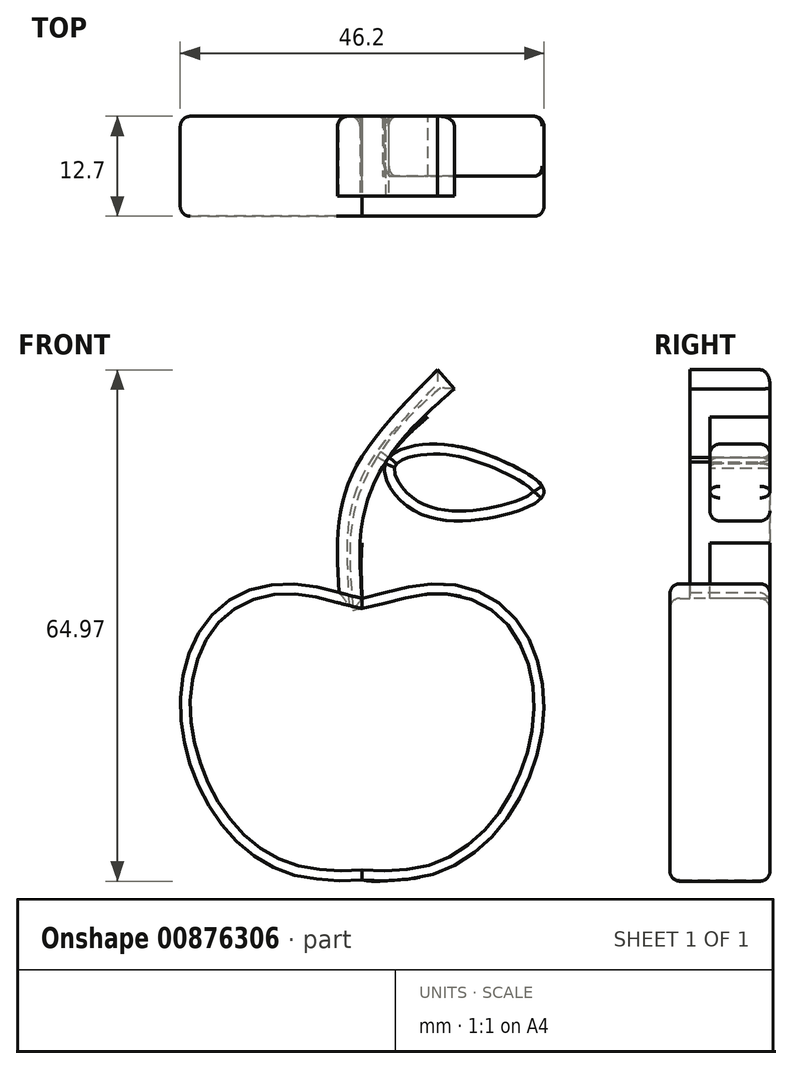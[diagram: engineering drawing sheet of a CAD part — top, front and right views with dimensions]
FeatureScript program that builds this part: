
annotation { "Feature Type Name" : "Feature", "Feature Type Description" : "" }
export const myFeature = defineFeature(function(context is Context, id is Id, definition is map)
    precondition{}
    {
        {
            var Q0;
            Q0=qCreatedBy(makeId("Front.planeOp"),FACE);
            var sketch = newSketch(context, id + "F0", { "sketchPlane" : qUnion([Q0])});
            skFitSpline(sketch, "E0", {"points": [v(0, 29.07) * mm, v(-9.03, 30.9) * mm, v(-18.51, 27.54) * mm, v(-23.1, 15) * mm, v(-17.6, 0) * mm, v(-9.64, -5.81) * mm, v(-4.44, -6.73) * mm, v(0, -6.73) * mm], "startDerivative": vector(-62.06, 12.6) * mm, "endDerivative": vector(36.3, 8.01) * mm});
            skFitSpline(sketch, "E1.MirrorCS", {"points": [v(0, 29.07) * mm, v(9.03, 30.9) * mm, v(18.51, 27.54) * mm, v(23.1, 15) * mm, v(17.6, 0) * mm, v(9.64, -5.81) * mm, v(4.44, -6.73) * mm, v(0, -6.73) * mm], "startDerivative": vector(62.06, 12.6) * mm, "endDerivative": vector(-36.3, 8.01) * mm});
            skFitSpline(sketch, "E2", {"points": [v(0, 29.07) * mm, v(0, 36.1) * mm, v(2.93, 46.2) * mm, v(9.03, 52.63) * mm], "startDerivative": vector(-1.25, 22) * mm, "endDerivative": vector(20.43, 16.63) * mm});
            skFitSpline(sketch, "E3", {"points": [v(2.93, 46.2) * mm, v(9.03, 48.65) * mm, v(18.51, 46.2) * mm, v(23.1, 42.53) * mm, v(17.29, 39.47) * mm, v(6.27, 40.39) * mm, v(2.93, 46.2) * mm]});
            skPoint(sketch, "E4.1.internal.orphan", {"position": v(-2.93, 36.1) * mm});
            skPoint(sketch, "E4.2.internal.orphan", {"position": v(0, 47.12) * mm});
            skPoint(sketch, "E4.3.internal.orphan", {"position": v(6.74, 56) * mm});
            skFitSpline(sketch, "E5", {"points": [v(9.6, 58.1) * mm, v(11.72, 55.65) * mm, v(9.03, 52.63) * mm, v(3.4, 46.96) * mm, v(0, 38.66) * mm, v(0, 29.07) * mm], "startDerivative": vector(22.53, -17) * mm, "endDerivative": vector(3.05, -39.95) * mm});
            skPoint(sketch, "E6.1.internal.orphan", {"position": v(-2.93, 38.79) * mm});
            skPoint(sketch, "E6.endDerivative.orphan", {"position": v(6.74, 55.65) * mm});
            skFitSpline(sketch, "E7", {"points": [v(-2.93, 29.66) * mm, v(-2.93, 38.79) * mm, v(0, 47.12) * mm, v(9.6, 58.1) * mm], "startDerivative": vector(-1.63, 29.49) * mm, "endDerivative": vector(28.3, 28.37) * mm});
            skFitSpline(sketch, "E8", {"points": [v(0, 29.07) * mm, v(0, 36.1) * mm, v(2.93, 46.2) * mm, v(11.72, 55.65) * mm], "startDerivative": vector(-1.18, 23.85) * mm, "endDerivative": vector(26.88, 23.3) * mm});
            skFitSpline(sketch, "E9", {"points": [v(11.72, 55.65) * mm, v(9.6, 58.1) * mm], "startDerivative": vector(-2.13, 2.44) * mm, "endDerivative": vector(-2.13, 2.44) * mm});
            skSolve(sketch);
        }
        {
            var Q0;
            {var subQ0=sQuery(id+"F0.wireOp",EDGE,"E1.MirrorCS");Q0=makeQuery(id+"F0.imprint","IMPRINT",FACE,{"disambiguationData":[TD([[makeQuery(id+"F0.imprint","IMPRINT",EDGE,{"derivedFrom":subQ0}),-1.0]])]});}
            extrude(context, id + "F1", {"entities" : qUnion([Q0]), "depth" : 12.7 * mm, "offsetDistance" : 25.4 * mm});
        }
        {
            var Q0;
            {var subQ0=sQuery(id+"F0.wireOp",EDGE,"E2");Q0=makeQuery(id+"F0.imprint","IMPRINT",FACE,{"disambiguationData":[TD([[makeQuery(id+"F0.imprint","IMPRINT",EDGE,{"derivedFrom":subQ0}),-1.0]])]});}
            extrude(context, id + "F2", {"entities" : qUnion([Q0]), "depth" : 7.62 * mm, "offsetDistance" : 25.4 * mm});
        }
        {
            var Q0;
            {var subQ4=sQuery(id+"F0.wireOp",EDGE,"E9");Q0=makeQuery(id+"F0.imprint","IMPRINT",FACE,{"disambiguationData":[TD([[makeQuery(id+"F0.imprint","IMPRINT",EDGE,{"derivedFrom":subQ4}),1.0]])]});}
            extrude(context, id + "F3", {"entities" : qUnion([Q0]), "operationType" : NewBodyOperationType.ADD, "depth" : 10.16 * mm, "offsetDistance" : 25.4 * mm});
        }
        {
            var Q0;
            Q0=makeQuery(id+"F1.opExtrude","CAP_FACE",FACE,{"disambiguationData":[OSD([sQuery(id+"F0.wireOp",EDGE,"E0"),sQuery(id+"F0.wireOp",EDGE,"E1.MirrorCS")])],"isStart":false});
            var Q1;
            Q1=makeQuery(id+"F1.opExtrude","CAP_EDGE",EDGE,{"disambiguationData":[OSD([sQuery(id+"F0.wireOp",EDGE,"E0")])],"isStart":true});
            var Q2;
            {var subQ0=sQuery(id+"F0.wireOp",EDGE,"E0");Q2=makeQuery(id+"F3.boolean.opBoolean","MERGE",FACE,{"derivedFrom":[makeQuery(id+"F1.opExtrude","CAP_FACE",FACE,{"disambiguationData":[OSD([subQ0,sQuery(id+"F0.wireOp",EDGE,"E1.MirrorCS")])],"isStart":true}),makeQuery(id+"F3.opExtrude","CAP_FACE",FACE,{"disambiguationData":[OSD([subQ0,sQuery(id+"F0.wireOp",EDGE,"E3"),sQuery(id+"F0.wireOp",EDGE,"E7"),sQuery(id+"F0.wireOp",EDGE,"E8"),sQuery(id+"F0.wireOp",EDGE,"E9")])],"isStart":true})]});}
            var Q3;
            Q3=makeQuery(id+"F2.opExtrude","CAP_FACE",FACE,{"disambiguationData":[OSD([sQuery(id+"F0.wireOp",EDGE,"E2"),sQuery(id+"F0.wireOp",EDGE,"E3")])],"isStart":true});
            var Q4;
            Q4=makeQuery(id+"F2.opExtrude","CAP_FACE",FACE,{"disambiguationData":[OSD([sQuery(id+"F0.wireOp",EDGE,"E2"),sQuery(id+"F0.wireOp",EDGE,"E3")])],"isStart":false});
            fillet(context, id + "F4", {"entities" : qUnion([Q0, Q1, Q2, Q3, Q4]), "radius" : 1.27 * mm, "tangentPropagation" : true, "allowEdgeOverflow" : false});
        }
    });
